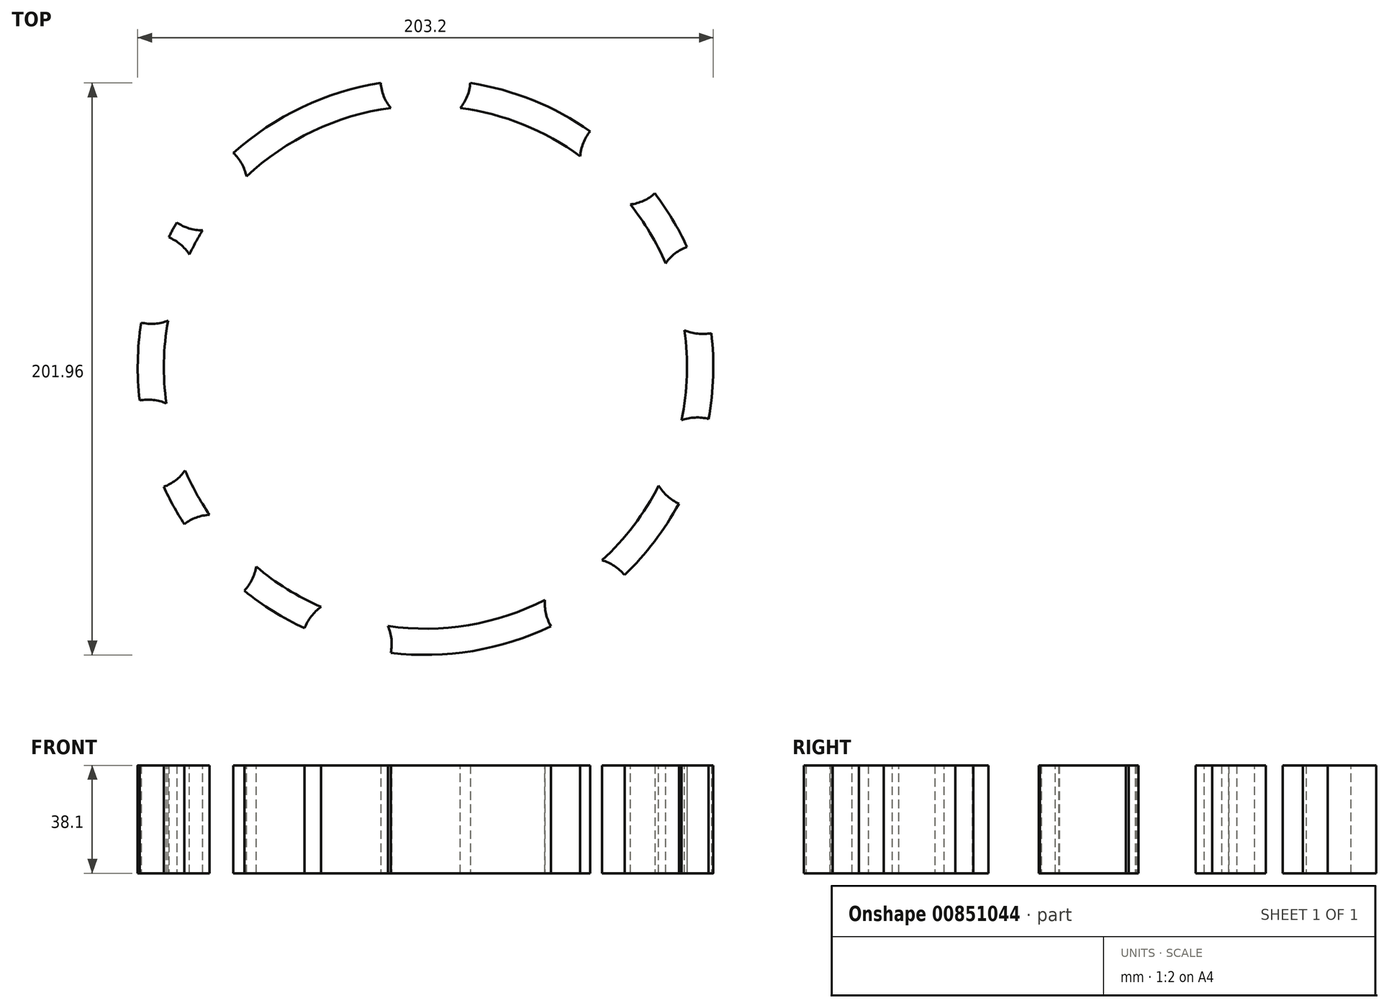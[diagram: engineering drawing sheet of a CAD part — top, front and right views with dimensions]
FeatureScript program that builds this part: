
annotation { "Feature Type Name" : "Feature", "Feature Type Description" : "" }
export const myFeature = defineFeature(function(context is Context, id is Id, definition is map)
    precondition{}
    {
        {
            var Q0;
            Q0=qCreatedBy(makeId("Top.planeOp"),FACE);
            var sketch = newSketch(context, id + "F0", { "sketchPlane" : qUnion([Q0])});
            skArc(sketch, "E0", {"start": v(-87.8, 51.13) * mm, "mid": v(-89.27, 48.52) * mm, "end": v(-90.66, 45.86) * mm});
            skArc(sketch, "E1", {"start": v(-87.8, 51.13) * mm, "mid": v(-66.46, 54.15) * mm, "end": v(-67.8, 75.66) * mm});
            skArc(sketch, "E2", {"start": v(-15.83, 100.36) * mm, "mid": v(0, 85.73) * mm, "end": v(15.83, 100.36) * mm});
            skArc(sketch, "E3", {"start": v(58.16, 83.3) * mm, "mid": v(59.42, 61.8) * mm, "end": v(80.97, 61.37) * mm});
            skArc(sketch, "E4", {"start": v(92.29, 42.49) * mm, "mid": v(82.5, 23.28) * mm, "end": v(100.89, 12.03) * mm});
            skArc(sketch, "E5", {"start": v(99.94, -18.3) * mm, "mid": v(80.89, -28.39) * mm, "end": v(89.46, -48.16) * mm});
            skArc(sketch, "E6", {"start": v(70.25, -73.4) * mm, "mid": v(48.9, -70.4) * mm, "end": v(44.26, -91.45) * mm});
            skArc(sketch, "E7", {"start": v(-12.26, -100.86) * mm, "mid": v(-23.47, -82.45) * mm, "end": v(-42.7, -92.2) * mm});
            skArc(sketch, "E8", {"start": v(-63.98, -78.93) * mm, "mid": v(-63.7, -57.37) * mm, "end": v(-85.16, -55.4) * mm});
            skArc(sketch, "E9", {"start": v(-92.4, -42.25) * mm, "mid": v(-82.56, -23.07) * mm, "end": v(-100.92, -11.77) * mm});
            skArc(sketch, "E10", {"start": v(-100.37, 15.74) * mm, "mid": v(-81.59, 26.3) * mm, "end": v(-90.66, 45.86) * mm});
            skCircle(sketch, "E11", {"center": v(-123.4, 46.72) * mm, "radius": 2.03 * mm});
            skArc(sketch, "E12.trimOffspring", {"start": v(-100.37, 15.74) * mm, "mid": v(-101.58, 2) * mm, "end": v(-100.92, -11.77) * mm});
            skArc(sketch, "E13.trimOffspring", {"start": v(-92.4, -42.25) * mm, "mid": v(-89.02, -48.96) * mm, "end": v(-85.16, -55.4) * mm});
            skArc(sketch, "E14.trimOffspring", {"start": v(-63.98, -78.93) * mm, "mid": v(-53.75, -86.22) * mm, "end": v(-42.7, -92.2) * mm});
            skArc(sketch, "E15.trimOffspring", {"start": v(-12.26, -100.86) * mm, "mid": v(16.68, -100.22) * mm, "end": v(44.26, -91.45) * mm});
            skArc(sketch, "E16.trimOffspring", {"start": v(70.25, -73.4) * mm, "mid": v(80.85, -61.53) * mm, "end": v(89.46, -48.16) * mm});
            skArc(sketch, "E17.trimOffspring", {"start": v(99.94, -18.3) * mm, "mid": v(101.55, -3.17) * mm, "end": v(100.89, 12.03) * mm});
            skArc(sketch, "E18.trimOffspring", {"start": v(92.29, 42.49) * mm, "mid": v(87.14, 52.24) * mm, "end": v(80.97, 61.37) * mm});
            skArc(sketch, "E19.trimOffspring", {"start": v(58.16, 83.3) * mm, "mid": v(37.96, 94.24) * mm, "end": v(15.83, 100.36) * mm});
            skArc(sketch, "E20.trimOffspring", {"start": v(-15.83, 100.36) * mm, "mid": v(-43.6, 91.77) * mm, "end": v(-67.8, 75.66) * mm});
            skSolve(sketch);
        }
        {
            var Q0;
            Q0=makeQuery(id+"F0.imprint","IMPRINT",FACE,{"disambiguationData":[TD([[makeQuery(id+"F0.imprint","IMPRINT",EDGE,{"derivedFrom":sQuery(id+"F0.wireOp",EDGE,"E0")}),1.0]])]});
            extrude(context, id + "F1", {"entities" : qUnion([Q0]), "depth" : 38.1 * mm, "offsetDistance" : 25.4 * mm});
        }
        {
            var Q0;
            Q0=makeQuery(id+"F1.opExtrude","CAP_FACE",FACE,{"disambiguationData":[OSD([sQuery(id+"F0.wireOp",EDGE,"E0")])],"isStart":false});
            var sketch = newSketch(context, id + "F2", { "sketchPlane" : qUnion([Q0])});
            skCircle(sketch, "E21", {"center": v(0, 0) * mm, "radius": 92.35 * mm});
            skSolve(sketch);
        }
        {
            var Q0;
            Q0=makeQuery(id+"F2.imprint","IMPRINT",FACE,{"disambiguationData":[TD([[makeQuery(id+"F2.imprint","IMPRINT",EDGE,{"derivedFrom":sQuery(id+"F2.wireOp",EDGE,"E21")}),1.0]])]});
            extrude(context, id + "F3", {"entities" : qUnion([Q0]), "operationType" : NewBodyOperationType.REMOVE, "oppositeDirection" : true, "depth" : 38.1 * mm, "offsetDistance" : 25.4 * mm});
        }
    });
